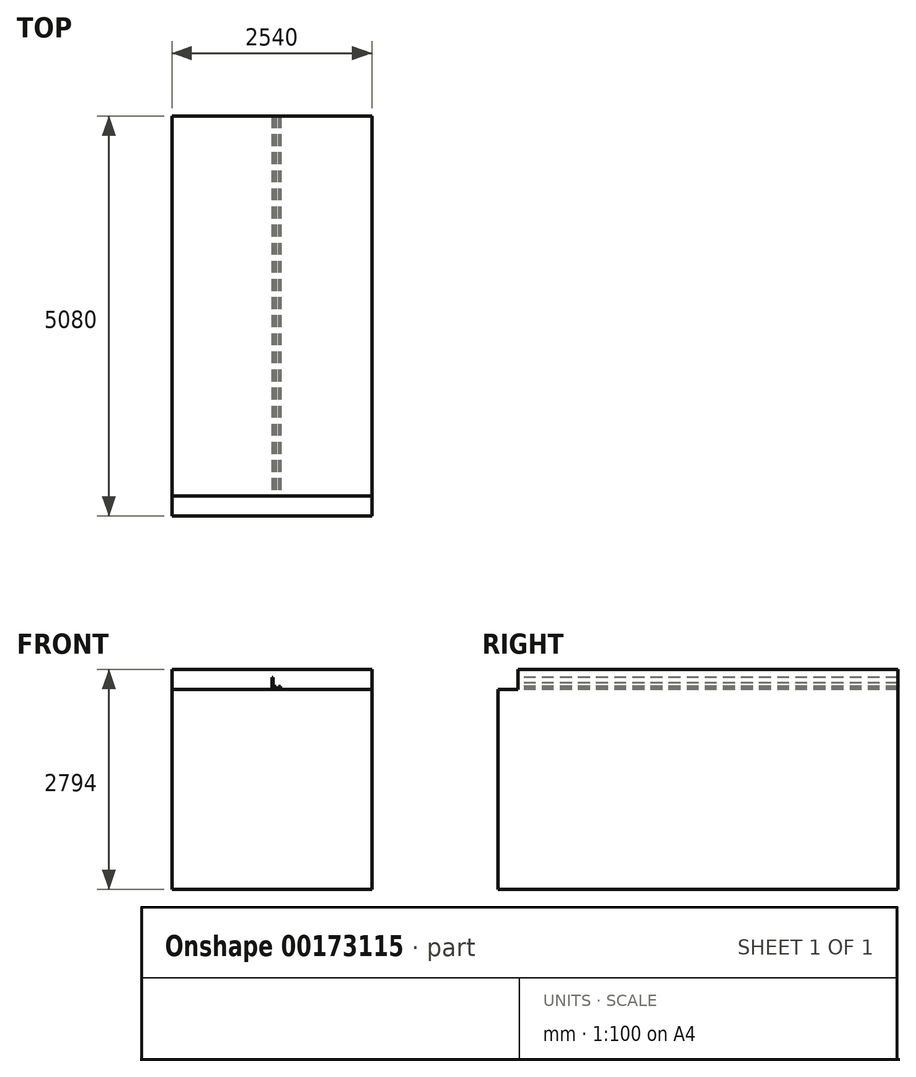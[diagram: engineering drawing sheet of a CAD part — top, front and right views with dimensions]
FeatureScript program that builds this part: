
annotation { "Feature Type Name" : "Feature", "Feature Type Description" : "" }
export const myFeature = defineFeature(function(context is Context, id is Id, definition is map)
    precondition{}
    {
        {
            var Q0;
            Q0=qCreatedBy(makeId("Front.planeOp"),FACE);
            var sketch = newSketch(context, id + "F0", { "sketchPlane" : qUnion([Q0])});
            skLineSegment(sketch, "E0", {"start": v(0, 0) * mm, "end": v(0, 149.86) * mm});
            skLineSegment(sketch, "E1", {"start": v(0, 149.86) * mm, "end": v(17.78, 149.86) * mm});
            skLineSegment(sketch, "E2", {"start": v(17.78, 149.86) * mm, "end": v(17.78, 22.86) * mm});
            skLineSegment(sketch, "E3", {"start": v(17.78, 22.86) * mm, "end": v(38.1, 22.86) * mm});
            skLineSegment(sketch, "E4", {"start": v(38.1, 22.86) * mm, "end": v(38.1, 35.56) * mm});
            skLineSegment(sketch, "E5", {"start": v(38.1, 35.56) * mm, "end": v(50.8, 35.56) * mm});
            skLineSegment(sketch, "E6", {"start": v(50.8, 35.56) * mm, "end": v(50.8, 10.16) * mm});
            skLineSegment(sketch, "E7", {"start": v(50.8, 10.16) * mm, "end": v(83.82, 10.16) * mm});
            skLineSegment(sketch, "E8", {"start": v(83.82, 10.16) * mm, "end": v(83.82, 35.56) * mm});
            skLineSegment(sketch, "E9", {"start": v(83.82, 35.56) * mm, "end": v(109.22, 35.56) * mm});
            skLineSegment(sketch, "E10", {"start": v(109.22, 35.56) * mm, "end": v(109.22, 0) * mm});
            skLineSegment(sketch, "E11", {"start": v(0, 0) * mm, "end": v(109.22, 0) * mm});
            skSolve(sketch);
        }
        {
            var Q0;
            Q0=qCreatedBy(makeId("Front.planeOp"),FACE);
            var sketch = newSketch(context, id + "F1", { "sketchPlane" : qUnion([Q0])});
            skLineSegment(sketch, "E12.bottom", {"start": v(-1270, 0) * mm, "end": v(1270, 0) * mm});
            skLineSegment(sketch, "E12.top", {"start": v(-1270, 254) * mm, "end": v(1270, 254) * mm});
            skLineSegment(sketch, "E12.left", {"start": v(-1270, 0) * mm, "end": v(-1270, 254) * mm});
            skLineSegment(sketch, "E12.right", {"start": v(1270, 0) * mm, "end": v(1270, 254) * mm});
            skSolve(sketch);
        }
        {
            var Q0;
            Q0=makeQuery(id+"F1.imprint","IMPRINT",FACE,{"disambiguationData":[TD([[makeQuery(id+"F1.imprint","IMPRINT",EDGE,{"derivedFrom":sQuery(id+"F1.wireOp",EDGE,"E12.bottom")}),1.0]])]});
            extrude(context, id + "F2", {"entities" : qUnion([Q0]), "oppositeDirection" : true, "depth" : 4826 * mm});
        }
        {
            var Q0;
            Q0=makeQuery(id+"F0.imprint","IMPRINT",FACE,{"disambiguationData":[TD([[makeQuery(id+"F0.imprint","IMPRINT",EDGE,{"derivedFrom":sQuery(id+"F0.wireOp",EDGE,"E0")}),-1.0]])]});
            extrude(context, id + "F3", {"entities" : qUnion([Q0]), "operationType" : NewBodyOperationType.REMOVE, "oppositeDirection" : true, "depth" : 4826 * mm});
        }
        {
            var Q0;
            Q0=makeQuery(id+"F2.opExtrude","SWEPT_FACE",FACE,{"disambiguationData":[OSD([sQuery(id+"F1.wireOp",EDGE,"E12.right")])]});
            var sketch = newSketch(context, id + "F4", { "sketchPlane" : qUnion([Q0])});
            skLineSegment(sketch, "E13.bottom", {"start": v(4826, 0) * mm, "end": v(-254, 0) * mm});
            skLineSegment(sketch, "E13.top", {"start": v(4826, -2540) * mm, "end": v(-254, -2540) * mm});
            skLineSegment(sketch, "E13.left", {"start": v(4826, 0) * mm, "end": v(4826, -2540) * mm});
            skLineSegment(sketch, "E13.right", {"start": v(-254, 0) * mm, "end": v(-254, -2540) * mm});
            skSolve(sketch);
        }
        {
            var Q0;
            Q0=makeQuery(id+"F4.imprint","IMPRINT",FACE,{"disambiguationData":[TD([[makeQuery(id+"F4.imprint","IMPRINT",EDGE,{"derivedFrom":sQuery(id+"F4.wireOp",EDGE,"E13.top")}),-1.0]])]});
            extrude(context, id + "F5", {"entities" : qUnion([Q0]), "operationType" : NewBodyOperationType.ADD, "oppositeDirection" : true, "depth" : 2540 * mm});
        }
        {
            var Q0;
            Q0=makeQuery(id+"F2.opExtrude","CAP_FACE",FACE,{"disambiguationData":[OSD([sQuery(id+"F1.wireOp",EDGE,"E12.bottom"),sQuery(id+"F1.wireOp",EDGE,"E12.top"),sQuery(id+"F1.wireOp",EDGE,"E12.left"),sQuery(id+"F1.wireOp",EDGE,"E12.right")])],"isStart":true});
            var sketch = newSketch(context, id + "F6", { "sketchPlane" : qUnion([Q0])});
            skLineSegment(sketch, "E14", {"start": v(6.35, 0) * mm, "end": v(6.35, 81.28) * mm});
            skLineSegment(sketch, "E15", {"start": v(6.35, 81.28) * mm, "end": v(11.43, 81.28) * mm});
            skLineSegment(sketch, "E16", {"start": v(11.43, 81.28) * mm, "end": v(11.43, 5.08) * mm});
            skLineSegment(sketch, "E17", {"start": v(11.43, 5.08) * mm, "end": v(87.63, 5.08) * mm});
            skLineSegment(sketch, "E18", {"start": v(87.63, 5.08) * mm, "end": v(87.63, 0) * mm});
            skLineSegment(sketch, "E19", {"start": v(6.35, 0) * mm, "end": v(87.63, 0) * mm});
            skSolve(sketch);
        }
        {
            var Q0;
            Q0=makeQuery(id+"F6.imprint","IMPRINT",FACE,{"disambiguationData":[TD([[makeQuery(id+"F6.imprint","IMPRINT",EDGE,{"derivedFrom":sQuery(id+"F6.wireOp",EDGE,"E14")}),-1.0]])]});
            extrude(context, id + "F7", {"entities" : qUnion([Q0]), "operationType" : NewBodyOperationType.ADD, "oppositeDirection" : true, "depth" : 4826 * mm});
        }
    });
